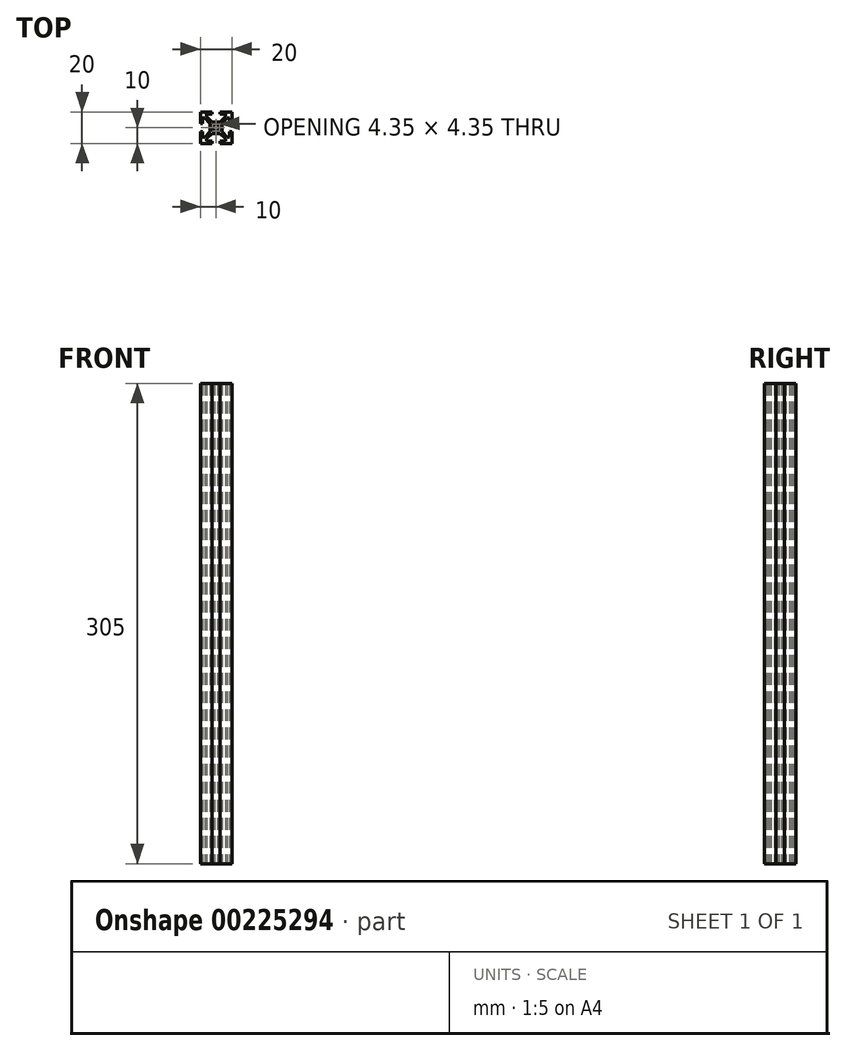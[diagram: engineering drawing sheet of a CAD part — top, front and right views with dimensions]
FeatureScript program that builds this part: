
annotation { "Feature Type Name" : "Feature", "Feature Type Description" : "" }
export const myFeature = defineFeature(function(context is Context, id is Id, definition is map)
    precondition{}
    {
        {
            var Q0;
            Q0=qCreatedBy(makeId("Top.planeOp"),FACE);
            var sketch = newSketch(context, id + "F0", { "sketchPlane" : qUnion([Q0])});
            skLineSegment(sketch, "E0.bottom", {"start": v(10, 10) * mm, "end": v(-10, 10) * mm});
            skLineSegment(sketch, "E0.top", {"start": v(10, -10) * mm, "end": v(-10, -10) * mm});
            skLineSegment(sketch, "E0.left", {"start": v(10, 10) * mm, "end": v(10, -10) * mm});
            skLineSegment(sketch, "E0.right", {"start": v(-10, 10) * mm, "end": v(-10, -10) * mm});
            skPoint(sketch, "E0.middle", {"position": v(0, 0) * mm});
            skLineSegment(sketch, "E1", {"start": v(-10, 10) * mm, "end": v(10, -10) * mm, "construction": true});
            skLineSegment(sketch, "E2", {"start": v(-10, -10) * mm, "end": v(10, 10) * mm, "construction": true});
            skLineSegment(sketch, "E3", {"start": v(0, 10) * mm, "end": v(0, -10) * mm, "construction": true});
            skLineSegment(sketch, "E4", {"start": v(-10, 0) * mm, "end": v(10, 0) * mm, "construction": true});
            skPoint(sketch, "E4.endSnap0", {"position": v(10, 0) * mm});
            skLineSegment(sketch, "E5", {"start": v(-2.63, 13.49) * mm, "end": v(2.63, 13.49) * mm});
            skLineSegment(sketch, "E6", {"start": v(2.63, 13.49) * mm, "end": v(2.63, 8.5) * mm});
            skLineSegment(sketch, "E7", {"start": v(2.63, 8.5) * mm, "end": v(6, 8.5) * mm});
            skLineSegment(sketch, "E8", {"start": v(6, 8.5) * mm, "end": v(6, 7.06) * mm});
            skLineSegment(sketch, "E9", {"start": v(6, 7.06) * mm, "end": v(2.6, 3.66) * mm});
            skLineSegment(sketch, "E10", {"start": v(2.6, 3.66) * mm, "end": v(-2.6, 3.66) * mm});
            skLineSegment(sketch, "E11", {"start": v(-2.6, 3.66) * mm, "end": v(-6, 7.06) * mm});
            skLineSegment(sketch, "E12", {"start": v(-6, 7.06) * mm, "end": v(-6, 8.5) * mm});
            skLineSegment(sketch, "E13", {"start": v(-6, 8.5) * mm, "end": v(-2.63, 8.5) * mm});
            skLineSegment(sketch, "E14", {"start": v(-2.63, 8.5) * mm, "end": v(-2.63, 13.49) * mm});
            skCircle(sketch, "E15", {"center": v(0, 0) * mm, "radius": 2.1 * mm});
            skLineSegment(sketch, "E16.MirrorCS", {"start": v(-7.06, 6) * mm, "end": v(-8.5, 6) * mm});
            skLineSegment(sketch, "E17.MirrorCS", {"start": v(-3.66, 2.6) * mm, "end": v(-7.06, 6) * mm});
            skLineSegment(sketch, "E18.MirrorCS", {"start": v(-8.5, 6) * mm, "end": v(-8.5, 2.63) * mm});
            skLineSegment(sketch, "E19.MirrorCS", {"start": v(-3.66, -2.6) * mm, "end": v(-3.66, 2.6) * mm});
            skLineSegment(sketch, "E20.MirrorCS", {"start": v(-7.06, -6) * mm, "end": v(-3.66, -2.6) * mm});
            skLineSegment(sketch, "E21.MirrorCS", {"start": v(-8.5, -6) * mm, "end": v(-7.06, -6) * mm});
            skLineSegment(sketch, "E22.MirrorCS", {"start": v(-8.5, -2.63) * mm, "end": v(-8.5, -6) * mm});
            skLineSegment(sketch, "E23.MirrorCS", {"start": v(-13.49, -2.63) * mm, "end": v(-8.5, -2.63) * mm});
            skLineSegment(sketch, "E24.MirrorCS", {"start": v(-13.49, 2.63) * mm, "end": v(-13.49, -2.63) * mm});
            skLineSegment(sketch, "E25.MirrorCS", {"start": v(-8.5, 2.63) * mm, "end": v(-13.49, 2.63) * mm});
            skLineSegment(sketch, "E26.MirrorCS", {"start": v(-2.6, -3.66) * mm, "end": v(-6, -7.06) * mm});
            skLineSegment(sketch, "E27.MirrorCS", {"start": v(2.6, -3.66) * mm, "end": v(-2.6, -3.66) * mm});
            skLineSegment(sketch, "E28.MirrorCS", {"start": v(6, -7.06) * mm, "end": v(2.6, -3.66) * mm});
            skLineSegment(sketch, "E29.MirrorCS", {"start": v(6, -8.5) * mm, "end": v(6, -7.06) * mm});
            skLineSegment(sketch, "E30.MirrorCS", {"start": v(2.63, -8.5) * mm, "end": v(6, -8.5) * mm});
            skLineSegment(sketch, "E31.MirrorCS", {"start": v(2.63, -13.49) * mm, "end": v(2.63, -8.5) * mm});
            skLineSegment(sketch, "E32.MirrorCS", {"start": v(-2.63, -13.49) * mm, "end": v(2.63, -13.49) * mm});
            skLineSegment(sketch, "E33.MirrorCS", {"start": v(-2.63, -8.5) * mm, "end": v(-2.63, -13.49) * mm});
            skLineSegment(sketch, "E34.MirrorCS", {"start": v(-6, -8.5) * mm, "end": v(-2.63, -8.5) * mm});
            skLineSegment(sketch, "E35.MirrorCS", {"start": v(-6, -7.06) * mm, "end": v(-6, -8.5) * mm});
            skLineSegment(sketch, "E36.MirrorCS", {"start": v(7.06, 6) * mm, "end": v(3.66, 2.6) * mm});
            skLineSegment(sketch, "E37.MirrorCS", {"start": v(8.5, 6) * mm, "end": v(7.06, 6) * mm});
            skLineSegment(sketch, "E38.MirrorCS", {"start": v(8.5, 2.63) * mm, "end": v(8.5, 6) * mm});
            skLineSegment(sketch, "E39.MirrorCS", {"start": v(13.49, 2.63) * mm, "end": v(8.5, 2.63) * mm});
            skLineSegment(sketch, "E40.MirrorCS", {"start": v(13.49, -2.63) * mm, "end": v(13.49, 2.63) * mm});
            skLineSegment(sketch, "E41.MirrorCS", {"start": v(8.5, -2.63) * mm, "end": v(13.49, -2.63) * mm});
            skLineSegment(sketch, "E42.MirrorCS", {"start": v(8.5, -6) * mm, "end": v(8.5, -2.63) * mm});
            skLineSegment(sketch, "E43.MirrorCS", {"start": v(7.06, -6) * mm, "end": v(8.5, -6) * mm});
            skLineSegment(sketch, "E44.MirrorCS", {"start": v(3.66, -2.6) * mm, "end": v(7.06, -6) * mm});
            skLineSegment(sketch, "E45.MirrorCS", {"start": v(3.66, 2.6) * mm, "end": v(3.66, -2.6) * mm});
            skCircle(sketch, "E46", {"center": v(-1.48, 1.48) * mm, "radius": 0.7 * mm});
            skCircle(sketch, "E47.MirrorC", {"center": v(1.48, 1.48) * mm, "radius": 0.7 * mm});
            skCircle(sketch, "E48.MirrorC", {"center": v(-1.48, -1.48) * mm, "radius": 0.7 * mm});
            skCircle(sketch, "E49.MirrorC", {"center": v(1.48, -1.48) * mm, "radius": 0.7 * mm});
            skSolve(sketch);
        }
        {
            var Q0;
            {var subQ29=sQuery(id+"F0.wireOp",EDGE,"E7");Q0=makeQuery(id+"F0.imprint","IMPRINT",FACE,{"disambiguationData":[TD([[makeQuery(id+"F0.imprint","IMPRINT",EDGE,{"derivedFrom":subQ29}),1.0]])]});}
            extrude(context, id + "F1", {"entities" : qUnion([Q0]), "depth" : 305 * mm});
        }
    });
